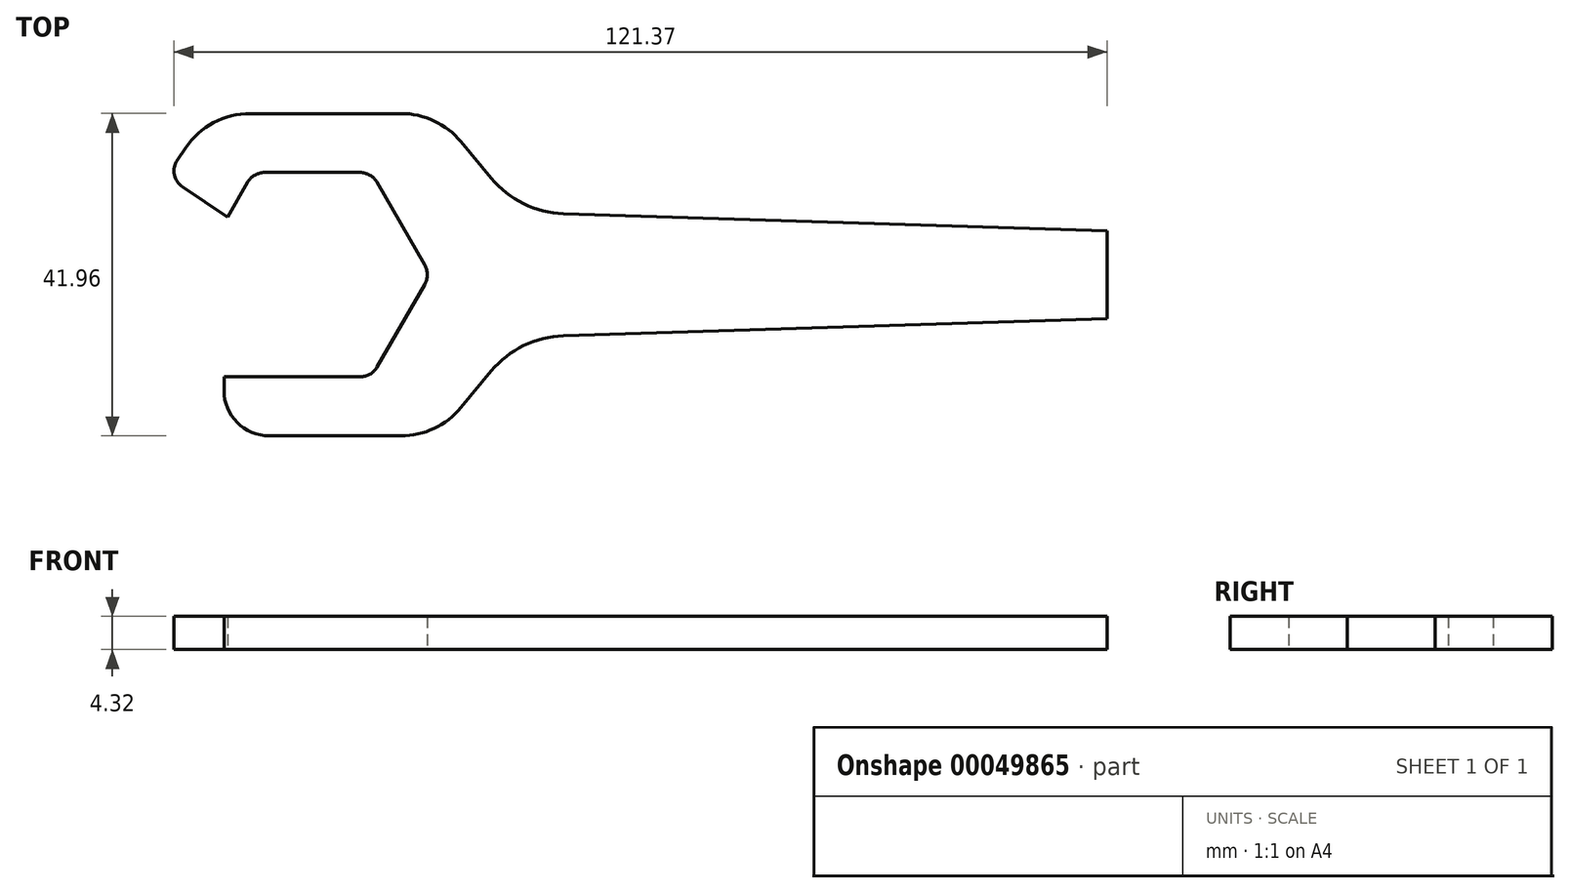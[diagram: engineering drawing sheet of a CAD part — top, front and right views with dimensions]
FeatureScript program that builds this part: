
annotation { "Feature Type Name" : "Feature", "Feature Type Description" : "" }
export const myFeature = defineFeature(function(context is Context, id is Id, definition is map)
    precondition{}
    {
        {
            var Q0;
            Q0=qCreatedBy(makeId("Top.planeOp"),FACE);
            var sketch = newSketch(context, id + "F0", { "sketchPlane" : qUnion([Q0])});
            skCircle(sketch, "E0.cCircle", {"center": v(0, 0) * mm, "radius": 13.3 * mm, "construction": true});
            skLineSegment(sketch, "E0.0", {"start": v(-6.21, 13.3) * mm, "end": v(6.21, 13.3) * mm});
            skLineSegment(sketch, "E0.1", {"start": v(8.41, 12.03) * mm, "end": v(14.62, 1.27) * mm});
            skLineSegment(sketch, "E0.2", {"start": v(14.62, -1.27) * mm, "end": v(8.41, -12.03) * mm});
            skLineSegment(sketch, "E0.3", {"start": v(6.21, -13.3) * mm, "end": v(-11.49, -13.3) * mm});
            skLineSegment(sketch, "E0.5", {"start": v(-11.52, 6.65) * mm, "end": v(-8.41, 12.03) * mm});
            skPoint(sketch, "E0.0.midPoint", {"position": v(0, 13.3) * mm});
            skLineSegment(sketch, "E1", {"start": v(-11.02, 7.45) * mm, "end": v(-16.87, 11.4) * mm});
            skLineSegment(sketch, "E2", {"start": v(-17.55, 14.93) * mm, "end": v(-16.48, 16.5) * mm});
            skLineSegment(sketch, "E3", {"start": v(-8.07, 20.98) * mm, "end": v(11.53, 20.98) * mm});
            skLineSegment(sketch, "E4", {"start": v(19.35, 17.3) * mm, "end": v(23.3, 12.54) * mm});
            skLineSegment(sketch, "E5", {"start": v(32.67, 7.95) * mm, "end": v(103.38, 5.7) * mm});
            skLineSegment(sketch, "E6", {"start": v(103.38, 5.7) * mm, "end": v(103.38, 0) * mm});
            skLineSegment(sketch, "E7.MirrorCS", {"start": v(103.38, -5.7) * mm, "end": v(103.38, 0) * mm});
            skLineSegment(sketch, "E8.MirrorCS", {"start": v(32.67, -7.95) * mm, "end": v(103.38, -5.7) * mm});
            skLineSegment(sketch, "E9.MirrorCS", {"start": v(-5.6, -20.98) * mm, "end": v(11.53, -20.98) * mm});
            skLineSegment(sketch, "E10.MirrorCS", {"start": v(19.35, -17.3) * mm, "end": v(23.3, -12.54) * mm});
            skLineSegment(sketch, "E11", {"start": v(-11.49, -13.3) * mm, "end": v(-11.49, -15.08) * mm});
            skPoint(sketch, "E12.orphan", {"position": v(-15.36, 0) * mm});
            skPoint(sketch, "E13.orphan", {"position": v(-13.46, -20.98) * mm});
            skPoint(sketch, "E14.visualSharp", {"position": v(-13.46, 20.98) * mm});
            skArc(sketch, "E14.filletArc", {"start": v(-8.07, 20.98) * mm, "mid": v(-12.83, 19.79) * mm, "end": v(-16.48, 16.5) * mm});
            skPoint(sketch, "E15.visualSharp", {"position": v(16.3, 20.98) * mm});
            skArc(sketch, "E15.filletArc", {"start": v(19.35, 17.3) * mm, "mid": v(15.85, 20.01) * mm, "end": v(11.53, 20.98) * mm});
            skPoint(sketch, "E16.visualSharp", {"position": v(16.3, -20.98) * mm});
            skArc(sketch, "E16.filletArc", {"start": v(11.53, -20.98) * mm, "mid": v(15.85, -20.01) * mm, "end": v(19.35, -17.3) * mm});
            skPoint(sketch, "E17.visualSharp", {"position": v(-11.49, -20.98) * mm});
            skArc(sketch, "E17.filletArc", {"start": v(-11.49, -15.08) * mm, "mid": v(-9.76, -19.25) * mm, "end": v(-5.6, -20.98) * mm});
            skPoint(sketch, "E18.visualSharp", {"position": v(-18.97, 12.82) * mm});
            skArc(sketch, "E18.filletArc", {"start": v(-17.55, 14.93) * mm, "mid": v(-17.94, 13.02) * mm, "end": v(-16.87, 11.4) * mm});
            skPoint(sketch, "E19.visualSharp", {"position": v(26.95, 8.13) * mm});
            skArc(sketch, "E19.filletArc", {"start": v(23.3, 12.54) * mm, "mid": v(27.5, 9.24) * mm, "end": v(32.67, 7.95) * mm});
            skPoint(sketch, "E20.visualSharp", {"position": v(26.95, -8.13) * mm});
            skArc(sketch, "E20.filletArc", {"start": v(32.67, -7.95) * mm, "mid": v(27.5, -9.24) * mm, "end": v(23.3, -12.54) * mm});
            skPoint(sketch, "E21.visualSharp", {"position": v(-7.68, 13.3) * mm});
            skArc(sketch, "E21.filletArc", {"start": v(-6.21, 13.3) * mm, "mid": v(-7.48, 12.96) * mm, "end": v(-8.41, 12.03) * mm});
            skPoint(sketch, "E22.visualSharp", {"position": v(7.68, 13.3) * mm});
            skArc(sketch, "E22.filletArc", {"start": v(8.41, 12.03) * mm, "mid": v(7.48, 12.96) * mm, "end": v(6.21, 13.3) * mm});
            skPoint(sketch, "E23.visualSharp", {"position": v(15.36, 0) * mm});
            skArc(sketch, "E23.filletArc", {"start": v(14.62, -1.27) * mm, "mid": v(14.96, 0) * mm, "end": v(14.62, 1.27) * mm});
            skPoint(sketch, "E24.visualSharp", {"position": v(7.68, -13.3) * mm});
            skArc(sketch, "E24.filletArc", {"start": v(6.21, -13.3) * mm, "mid": v(7.48, -12.96) * mm, "end": v(8.41, -12.03) * mm});
            skSolve(sketch);
        }
        {
            var Q0;
            Q0=makeQuery(id+"F0.imprint","IMPRINT",FACE,{"disambiguationData":[TD([[makeQuery(id+"F0.imprint","IMPRINT",EDGE,{"derivedFrom":sQuery(id+"F0.wireOp",EDGE,"E0.0")}),1.0]])]});
            extrude(context, id + "F1", {"entities" : qUnion([Q0]), "depth" : 4.32 * mm});
        }
    });
